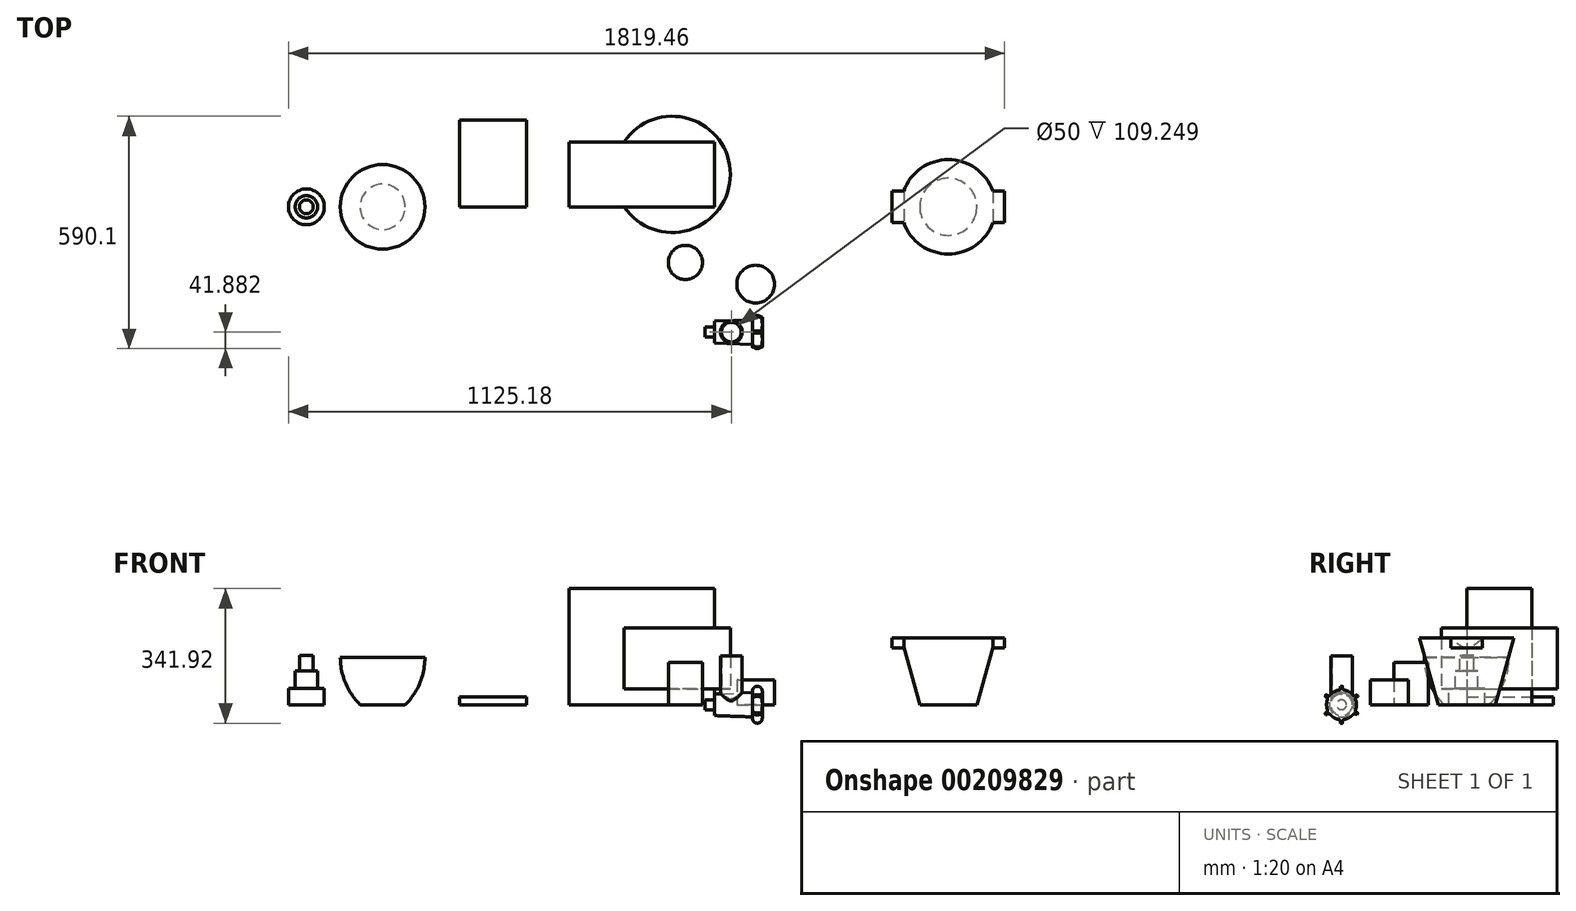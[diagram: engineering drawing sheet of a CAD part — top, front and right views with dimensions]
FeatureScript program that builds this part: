
annotation { "Feature Type Name" : "Feature", "Feature Type Description" : "" }
export const myFeature = defineFeature(function(context is Context, id is Id, definition is map)
    precondition{}
    {
        {
            var Q0;
            Q0=qCreatedBy(makeId("Top.planeOp"),FACE);
            var sketch = newSketch(context, id + "F0", { "sketchPlane" : qUnion([Q0])});
            skLineSegment(sketch, "E0.bottom", {"start": v(-647.77, 0) * mm, "end": v(-477.77, 0) * mm});
            skLineSegment(sketch, "E0.top", {"start": v(-647.77, 220) * mm, "end": v(-477.77, 220) * mm});
            skLineSegment(sketch, "E0.left", {"start": v(-647.77, 0) * mm, "end": v(-647.77, 220) * mm});
            skLineSegment(sketch, "E0.right", {"start": v(-477.77, 0) * mm, "end": v(-477.77, 220) * mm});
            skSolve(sketch);
        }
        {
            var Q0;
            Q0 = qSketchRegion(id + "F0", true);
            extrude(context, id + "F1", {"entities" : qUnion([Q0]), "depth" : 20 * mm});
        }
        {
            var Q0;
            Q0=qCreatedBy(makeId("Top.planeOp"),FACE);
            var sketch = newSketch(context, id + "F2", { "sketchPlane" : qUnion([Q0])});
            skLineSegment(sketch, "E1.bottom", {"start": v(0, 0) * mm, "end": v(-370, 0) * mm});
            skLineSegment(sketch, "E1.top", {"start": v(0, 165) * mm, "end": v(-370, 165) * mm});
            skLineSegment(sketch, "E1.left", {"start": v(0, 0) * mm, "end": v(0, 165) * mm});
            skLineSegment(sketch, "E1.right", {"start": v(-370, 0) * mm, "end": v(-370, 165) * mm});
            skSolve(sketch);
        }
        {
            var Q0;
            Q0 = qSketchRegion(id + "F2", true);
            extrude(context, id + "F3", {"entities" : qUnion([Q0]), "depth" : 40 * mm});
        }
        {
            var Q0;
            Q0=makeQuery(id+"F3.opExtrude","CAP_FACE",FACE,{"disambiguationData":[OSD([sQuery(id+"F2.wireOp",EDGE,"E1.bottom"),sQuery(id+"F2.wireOp",EDGE,"E1.top"),sQuery(id+"F2.wireOp",EDGE,"E1.left"),sQuery(id+"F2.wireOp",EDGE,"E1.right")])],"isStart":false});
            var sketch = newSketch(context, id + "F4", { "sketchPlane" : qUnion([Q0])});
            skArc(sketch, "E2", {"start": v(-229.77, 0) * mm, "mid": v(40, 82.5) * mm, "end": v(-229.77, 165) * mm});
            skLineSegment(sketch, "E3", {"start": v(0, 82.5) * mm, "end": v(-370, 82.5) * mm, "construction": true});
            skLineSegment(sketch, "E4", {"start": v(-229.77, 165) * mm, "end": v(-370, 165) * mm});
            skLineSegment(sketch, "E5", {"start": v(-370, 165) * mm, "end": v(-370, 0) * mm});
            skLineSegment(sketch, "E6", {"start": v(-370, 0) * mm, "end": v(-229.77, 0) * mm});
            skSolve(sketch);
        }
        {
            var Q0;
            Q0 = qSketchRegion(id + "F4", true);
            extrude(context, id + "F5", {"entities" : qUnion([Q0]), "operationType" : NewBodyOperationType.ADD, "depth" : 155 * mm});
        }
        {
            var Q0;
            Q0=makeQuery(id+"F5.opExtrude","CAP_FACE",FACE,{"disambiguationData":[OSD([sQuery(id+"F4.wireOp",EDGE,"E2"),sQuery(id+"F4.wireOp",EDGE,"E4"),sQuery(id+"F4.wireOp",EDGE,"E5"),sQuery(id+"F4.wireOp",EDGE,"E6")])],"isStart":false});
            var sketch = newSketch(context, id + "F6", { "sketchPlane" : qUnion([Q0])});
            skLineSegment(sketch, "E7.bottom", {"start": v(-370, 0) * mm, "end": v(0, 0) * mm});
            skLineSegment(sketch, "E7.top", {"start": v(-370, 165) * mm, "end": v(0, 165) * mm});
            skLineSegment(sketch, "E7.left", {"start": v(-370, 0) * mm, "end": v(-370, 165) * mm});
            skLineSegment(sketch, "E7.right", {"start": v(0, 0) * mm, "end": v(0, 165) * mm});
            skSolve(sketch);
        }
        {
            var Q0;
            Q0 = qSketchRegion(id + "F6", true);
            extrude(context, id + "F7", {"entities" : qUnion([Q0]), "operationType" : NewBodyOperationType.ADD, "depth" : 100 * mm});
        }
        {
            var Q0;
            Q0=qCreatedBy(makeId("Front.planeOp"),FACE);
            var sketch = newSketch(context, id + "F8", { "sketchPlane" : qUnion([Q0])});
            skLineSegment(sketch, "E8", {"start": v(593.64, 0) * mm, "end": v(593.64, 170) * mm});
            skLineSegment(sketch, "E9", {"start": v(593.64, 170) * mm, "end": v(713.64, 170) * mm});
            skLineSegment(sketch, "E10", {"start": v(713.64, 170) * mm, "end": v(666.14, 0) * mm});
            skLineSegment(sketch, "E11", {"start": v(666.14, 0) * mm, "end": v(593.64, 0) * mm});
            skSolve(sketch);
        }
        {
            var Q0;
            Q0=makeQuery(id+"F8.imprint","IMPRINT",FACE,{"disambiguationData":[TD([[makeQuery(id+"F8.imprint","IMPRINT",EDGE,{"derivedFrom":sQuery(id+"F8.wireOp",EDGE,"E8")}),-1.0]])]});
            var Q1;
            Q1=sQuery(id+"F8.wireOp",EDGE,"E8");
            revolve(context, id + "F9", {"entities" : qUnion([Q0]), "axis" : qUnion([Q1]), "revolveType" : RevolveType.FULL});
        }
        {
            var Q0;
            Q0=makeQuery(id+"F9.opRevolve","SWEPT_FACE",FACE,{"disambiguationData":[OSD([sQuery(id+"F8.wireOp",EDGE,"E9")])]});
            var sketch = newSketch(context, id + "F10", { "sketchPlane" : qUnion([Q0])});
            skLineSegment(sketch, "E12.bottom", {"start": v(480.5, 40) * mm, "end": v(450.5, 40) * mm});
            skLineSegment(sketch, "E12.top", {"start": v(480.5, -40) * mm, "end": v(450.5, -40) * mm});
            skLineSegment(sketch, "E12.left", {"start": v(480.5, 40) * mm, "end": v(480.5, -40) * mm});
            skLineSegment(sketch, "E12.right", {"start": v(450.5, 40) * mm, "end": v(450.5, -40) * mm});
            skLineSegment(sketch, "E13", {"start": v(593.64, 120) * mm, "end": v(593.64, -120) * mm, "construction": true});
            skLineSegment(sketch, "E14.MirrorCS", {"start": v(706.78, -40) * mm, "end": v(736.78, -40) * mm});
            skLineSegment(sketch, "E15.MirrorCS", {"start": v(706.78, 40) * mm, "end": v(706.78, -40) * mm});
            skLineSegment(sketch, "E16.MirrorCS", {"start": v(736.78, 40) * mm, "end": v(736.78, -40) * mm});
            skLineSegment(sketch, "E17.MirrorCS", {"start": v(706.78, 40) * mm, "end": v(736.78, 40) * mm});
            skSolve(sketch);
        }
        {
            var Q0;
            Q0 = qSketchRegion(id + "F10", true);
            extrude(context, id + "F11", {"entities" : qUnion([Q0]), "operationType" : NewBodyOperationType.ADD, "oppositeDirection" : true, "depth" : 25 * mm});
        }
        {
            var Q0;
            Q0=qCreatedBy(makeId("Top.planeOp"),FACE);
            var sketch = newSketch(context, id + "F12", { "sketchPlane" : qUnion([Q0])});
            skCircle(sketch, "E18", {"center": v(-74.2, -141.42) * mm, "radius": 43.5 * mm});
            skSolve(sketch);
        }
        {
            var Q0;
            Q0 = qSketchRegion(id + "F12", true);
            extrude(context, id + "F13", {"entities" : qUnion([Q0]), "depth" : 108 * mm});
        }
        {
            var Q0;
            Q0=qCreatedBy(makeId("Top.planeOp"),FACE);
            var sketch = newSketch(context, id + "F14", { "sketchPlane" : qUnion([Q0])});
            skCircle(sketch, "E19", {"center": v(104.26, -196.52) * mm, "radius": 48 * mm});
            skSolve(sketch);
        }
        {
            var Q0;
            Q0 = qSketchRegion(id + "F14", true);
            extrude(context, id + "F15", {"entities" : qUnion([Q0]), "depth" : 63 * mm});
        }
        {
            var Q0;
            Q0=qCreatedBy(makeId("Right.planeOp"),FACE);
            var sketch = newSketch(context, id + "F16", { "sketchPlane" : qUnion([Q0])});
            skCircle(sketch, "E20", {"center": v(-318.22, 0) * mm, "radius": 27.5 * mm});
            skSolve(sketch);
        }
        {
            var Q0;
            Q0=qCreatedBy(makeId("Right.planeOp"),FACE);
            cPlane(context, id + "F17", {"entities" : qUnion([Q0]), "cplaneType" : CPlaneType.OFFSET, "offset" : 96 * mm, "width" : 150 * mm, "height" : 150 * mm});
        }
        {
            var Q0;
            Q0=sQuery(id+"F16.wireOp",VERTEX,"E20.center");
            var Q1;
            Q1=qCreatedBy(makeId("Front.planeOp"),FACE);
            cPlane(context, id + "F18", {"entities" : qUnion([Q0, Q1]), "cplaneType" : CPlaneType.PLANE_POINT, "offset" : 25 * mm, "width" : 150 * mm, "height" : 150 * mm});
        }
        {
            var Q0;
            Q0=qCreatedBy(id+"F17.planeOp",FACE);
            var sketch = newSketch(context, id + "F19", { "sketchPlane" : qUnion([Q0])});
            skCircle(sketch, "E21", {"center": v(-318.22, 0) * mm, "radius": 31 * mm});
            skSolve(sketch);
        }
        {
            var Q0;
            Q0=makeQuery(id+"F16.imprint","IMPRINT",FACE,{"disambiguationData":[TD([[makeQuery(id+"F16.imprint","IMPRINT",EDGE,{"derivedFrom":sQuery(id+"F16.wireOp",EDGE,"E20")}),1.0]])]});
            var Q1;
            Q1=makeQuery(id+"F19.imprint","IMPRINT",FACE,{"disambiguationData":[TD([[makeQuery(id+"F19.imprint","IMPRINT",EDGE,{"derivedFrom":sQuery(id+"F19.wireOp",EDGE,"E21")}),1.0]])]});
            loft(context, id + "F20", {"sheetProfilesArray" : [{ "sheetProfileEntities" : qUnion([Q0]) }, { "sheetProfileEntities" : qUnion([Q1]) }]});
        }
        {
            var Q0;
            Q0=makeQuery(id+"F20.opLoft","CAP_FACE",FACE,{"disambiguationData":[OSD([makeQuery(id+"F19.imprint","IMPRINT",FACE,{"disambiguationData":[TD([[makeQuery(id+"F19.imprint","IMPRINT",EDGE,{"derivedFrom":sQuery(id+"F19.wireOp",EDGE,"E21")}),1.0]])]})])],"isStart":true});
            var sketch = newSketch(context, id + "F21", { "sketchPlane" : qUnion([Q0])});
            skArc(sketch, "E22", {"start": v(-320.72, 37.92) * mm, "mid": v(-337.22, 32.9) * mm, "end": v(-349.8, 21.12) * mm});
            skLineSegment(sketch, "E23", {"start": v(-320.72, 37.92) * mm, "end": v(-320.72, 46.92) * mm});
            skLineSegment(sketch, "E24", {"start": v(-320.72, 46.92) * mm, "end": v(-315.72, 46.92) * mm});
            skLineSegment(sketch, "E25", {"start": v(-315.72, 46.92) * mm, "end": v(-315.72, 37.92) * mm});
            skLineSegment(sketch, "E26.1.0", {"start": v(-352.3, 16.8) * mm, "end": v(-360.1, 21.3) * mm});
            skLineSegment(sketch, "E26.1.1", {"start": v(-360.1, 21.3) * mm, "end": v(-357.6, 25.62) * mm});
            skLineSegment(sketch, "E26.1.2", {"start": v(-357.6, 25.62) * mm, "end": v(-349.8, 21.12) * mm});
            skLineSegment(sketch, "E26.2.0", {"start": v(-349.8, -21.12) * mm, "end": v(-357.6, -25.62) * mm});
            skLineSegment(sketch, "E26.2.1", {"start": v(-357.6, -25.62) * mm, "end": v(-360.1, -21.3) * mm});
            skLineSegment(sketch, "E26.2.2", {"start": v(-360.1, -21.3) * mm, "end": v(-352.3, -16.8) * mm});
            skLineSegment(sketch, "E26.3.0", {"start": v(-315.72, -37.92) * mm, "end": v(-315.72, -46.92) * mm});
            skLineSegment(sketch, "E26.3.1", {"start": v(-315.72, -46.92) * mm, "end": v(-320.72, -46.92) * mm});
            skLineSegment(sketch, "E26.3.2", {"start": v(-320.72, -46.92) * mm, "end": v(-320.72, -37.92) * mm});
            skLineSegment(sketch, "E26.4.0", {"start": v(-284.13, -16.8) * mm, "end": v(-276.34, -21.3) * mm});
            skLineSegment(sketch, "E26.4.1", {"start": v(-276.34, -21.3) * mm, "end": v(-278.84, -25.62) * mm});
            skLineSegment(sketch, "E26.4.2", {"start": v(-278.84, -25.62) * mm, "end": v(-286.63, -21.12) * mm});
            skLineSegment(sketch, "E26.5.0", {"start": v(-286.63, 21.12) * mm, "end": v(-278.84, 25.62) * mm});
            skLineSegment(sketch, "E26.5.1", {"start": v(-278.84, 25.62) * mm, "end": v(-276.34, 21.3) * mm});
            skLineSegment(sketch, "E26.5.2", {"start": v(-276.34, 21.3) * mm, "end": v(-284.13, 16.8) * mm});
            skArc(sketch, "E27.trimOffspring", {"start": v(-352.3, 16.8) * mm, "mid": v(-356.22, 0) * mm, "end": v(-352.3, -16.8) * mm});
            skArc(sketch, "E28.trimOffspring", {"start": v(-349.8, -21.12) * mm, "mid": v(-337.22, -32.9) * mm, "end": v(-320.72, -37.92) * mm});
            skArc(sketch, "E29.trimOffspring", {"start": v(-315.72, -37.92) * mm, "mid": v(-299.22, -32.9) * mm, "end": v(-286.63, -21.12) * mm});
            skArc(sketch, "E30.trimOffspring", {"start": v(-284.13, -16.8) * mm, "mid": v(-280.22, 0) * mm, "end": v(-284.13, 16.8) * mm});
            skArc(sketch, "E31.trimOffspring", {"start": v(-286.63, 21.12) * mm, "mid": v(-299.22, 32.9) * mm, "end": v(-315.72, 37.92) * mm});
            skSolve(sketch);
        }
        {
            var Q0;
            Q0 = qSketchRegion(id + "F21", true);
            extrude(context, id + "F22", {"entities" : qUnion([Q0]), "operationType" : NewBodyOperationType.ADD, "depth" : 25 * mm});
        }
        {
            var Q0;
            Q0=makeQuery(id+"F22.opExtrude","CAP_EDGE",EDGE,{"disambiguationData":[OSD([sQuery(id+"F21.wireOp",EDGE,"E26.1.1")])],"isStart":true});
            var Q1;
            Q1=makeQuery(id+"F22.opExtrude","CAP_EDGE",EDGE,{"disambiguationData":[OSD([sQuery(id+"F21.wireOp",EDGE,"E26.1.1")])],"isStart":false});
            var Q2;
            Q2=makeQuery(id+"F22.opExtrude","CAP_EDGE",EDGE,{"disambiguationData":[OSD([sQuery(id+"F21.wireOp",EDGE,"E26.2.1")])],"isStart":true});
            var Q3;
            Q3=makeQuery(id+"F22.opExtrude","CAP_EDGE",EDGE,{"disambiguationData":[OSD([sQuery(id+"F21.wireOp",EDGE,"E26.2.1")])],"isStart":false});
            var Q4;
            Q4=makeQuery(id+"F22.opExtrude","CAP_EDGE",EDGE,{"disambiguationData":[OSD([sQuery(id+"F21.wireOp",EDGE,"E26.3.1")])],"isStart":false});
            var Q5;
            Q5=makeQuery(id+"F22.opExtrude","CAP_EDGE",EDGE,{"disambiguationData":[OSD([sQuery(id+"F21.wireOp",EDGE,"E26.3.1")])],"isStart":true});
            var Q6;
            Q6=makeQuery(id+"F22.opExtrude","CAP_EDGE",EDGE,{"disambiguationData":[OSD([sQuery(id+"F21.wireOp",EDGE,"E26.4.1")])],"isStart":true});
            var Q7;
            Q7=makeQuery(id+"F22.opExtrude","CAP_EDGE",EDGE,{"disambiguationData":[OSD([sQuery(id+"F21.wireOp",EDGE,"E26.4.1")])],"isStart":false});
            var Q8;
            Q8=makeQuery(id+"F22.opExtrude","CAP_EDGE",EDGE,{"disambiguationData":[OSD([sQuery(id+"F21.wireOp",EDGE,"E26.5.1")])],"isStart":true});
            var Q9;
            Q9=makeQuery(id+"F22.opExtrude","CAP_EDGE",EDGE,{"disambiguationData":[OSD([sQuery(id+"F21.wireOp",EDGE,"E26.5.1")])],"isStart":false});
            var Q10;
            Q10=makeQuery(id+"F22.opExtrude","CAP_EDGE",EDGE,{"disambiguationData":[OSD([sQuery(id+"F21.wireOp",EDGE,"E24")])],"isStart":true});
            var Q11;
            Q11=makeQuery(id+"F22.opExtrude","CAP_EDGE",EDGE,{"disambiguationData":[OSD([sQuery(id+"F21.wireOp",EDGE,"E24")])],"isStart":false});
            fillet(context, id + "F23", {"entities" : qUnion([Q0, Q1, Q2, Q3, Q4, Q5, Q6, Q7, Q8, Q9, Q10, Q11]), "radius" : (25 / 2) * mm, "tangentPropagation" : true, "allowEdgeOverflow" : false});
        }
        {
            var Q0;
            Q0=makeQuery(id+"F22.opExtrude","SWEPT_EDGE",EDGE,{"disambiguationData":[OSD([sQuery(id+"F21.wireOp",EDGE,"E26.2.2"),sQuery(id+"F21.wireOp",EDGE,"E27.trimOffspring")])]});
            var Q1;
            Q1=makeQuery(id+"F22.opExtrude","SWEPT_EDGE",EDGE,{"disambiguationData":[OSD([sQuery(id+"F21.wireOp",EDGE,"E26.1.0"),sQuery(id+"F21.wireOp",EDGE,"E27.trimOffspring")])]});
            var Q2;
            Q2=makeQuery(id+"F22.opExtrude","SWEPT_EDGE",EDGE,{"disambiguationData":[OSD([sQuery(id+"F21.wireOp",EDGE,"E22"),sQuery(id+"F21.wireOp",EDGE,"E26.1.2")])]});
            var Q3;
            Q3=makeQuery(id+"F22.opExtrude","SWEPT_EDGE",EDGE,{"disambiguationData":[OSD([sQuery(id+"F21.wireOp",EDGE,"E22"),sQuery(id+"F21.wireOp",EDGE,"E23")])]});
            var Q4;
            Q4=makeQuery(id+"F22.opExtrude","SWEPT_EDGE",EDGE,{"disambiguationData":[OSD([sQuery(id+"F21.wireOp",EDGE,"E25"),sQuery(id+"F21.wireOp",EDGE,"E31.trimOffspring")])]});
            var Q5;
            Q5=makeQuery(id+"F22.opExtrude","SWEPT_EDGE",EDGE,{"disambiguationData":[OSD([sQuery(id+"F21.wireOp",EDGE,"E26.5.0"),sQuery(id+"F21.wireOp",EDGE,"E31.trimOffspring")])]});
            var Q6;
            Q6=makeQuery(id+"F22.opExtrude","SWEPT_EDGE",EDGE,{"disambiguationData":[OSD([sQuery(id+"F21.wireOp",EDGE,"E26.5.2"),sQuery(id+"F21.wireOp",EDGE,"E30.trimOffspring")])]});
            var Q7;
            Q7=makeQuery(id+"F22.opExtrude","SWEPT_EDGE",EDGE,{"disambiguationData":[OSD([sQuery(id+"F21.wireOp",EDGE,"E26.4.0"),sQuery(id+"F21.wireOp",EDGE,"E30.trimOffspring")])]});
            var Q8;
            Q8=makeQuery(id+"F22.opExtrude","SWEPT_EDGE",EDGE,{"disambiguationData":[OSD([sQuery(id+"F21.wireOp",EDGE,"E26.4.2"),sQuery(id+"F21.wireOp",EDGE,"E29.trimOffspring")])]});
            var Q9;
            Q9=makeQuery(id+"F22.opExtrude","SWEPT_EDGE",EDGE,{"disambiguationData":[OSD([sQuery(id+"F21.wireOp",EDGE,"E26.3.0"),sQuery(id+"F21.wireOp",EDGE,"E29.trimOffspring")])]});
            var Q10;
            Q10=makeQuery(id+"F22.opExtrude","SWEPT_EDGE",EDGE,{"disambiguationData":[OSD([sQuery(id+"F21.wireOp",EDGE,"E26.3.2"),sQuery(id+"F21.wireOp",EDGE,"E28.trimOffspring")])]});
            var Q11;
            Q11=makeQuery(id+"F22.opExtrude","SWEPT_EDGE",EDGE,{"disambiguationData":[OSD([sQuery(id+"F21.wireOp",EDGE,"E26.2.0"),sQuery(id+"F21.wireOp",EDGE,"E28.trimOffspring")])]});
            fillet(context, id + "F24", {"entities" : qUnion([Q0, Q1, Q2, Q3, Q4, Q5, Q6, Q7, Q8, Q9, Q10, Q11]), "radius" : 5 * mm, "tangentPropagation" : true, "allowEdgeOverflow" : false});
        }
        {
            var Q0;
            Q0=makeQuery(id+"F20.opLoft","CAP_FACE",FACE,{"disambiguationData":[OSD([makeQuery(id+"F16.imprint","IMPRINT",FACE,{"disambiguationData":[TD([[makeQuery(id+"F16.imprint","IMPRINT",EDGE,{"derivedFrom":sQuery(id+"F16.wireOp",EDGE,"E20")}),1.0]])]})])],"isStart":true});
            var sketch = newSketch(context, id + "F25", { "sketchPlane" : qUnion([Q0])});
            skCircle(sketch, "E32", {"center": v(318.22, 0) * mm, "radius": 12.5 * mm});
            skSolve(sketch);
        }
        {
            var Q0;
            Q0 = qSketchRegion(id + "F25", true);
            extrude(context, id + "F26", {"entities" : qUnion([Q0]), "operationType" : NewBodyOperationType.ADD, "depth" : 25 * mm});
        }
        {
            var Q0;
            Q0=qCreatedBy(makeId("Top.planeOp"),FACE);
            var sketch = newSketch(context, id + "F27", { "sketchPlane" : qUnion([Q0])});
            skCircle(sketch, "E33", {"center": v(42.5, -318.22) * mm, "radius": 27.5 * mm});
            skCircle(sketch, "E34", {"center": v(42.5, -318.22) * mm, "radius": 25 * mm});
            skSolve(sketch);
        }
        {
            var Q0;
            Q0 = qSketchRegion(id + "F27", true);
            extrude(context, id + "F28", {"entities" : qUnion([Q0]), "operationType" : NewBodyOperationType.ADD, "depth" : (97 + 54 / 2) * mm});
        }
        {
            var Q0;
            Q0=qCreatedBy(makeId("Front.planeOp"),FACE);
            var sketch = newSketch(context, id + "F29", { "sketchPlane" : qUnion([Q0])});
            skLineSegment(sketch, "E35", {"start": v(-843.41, 0) * mm, "end": v(-900.91, 0) * mm});
            skLineSegment(sketch, "E36", {"start": v(-950.91, 120) * mm, "end": v(-843.41, 120) * mm});
            skLineSegment(sketch, "E37", {"start": v(-843.41, 120) * mm, "end": v(-843.41, 0) * mm});
            skArc(sketch, "E38", {"start": v(-950.91, 120) * mm, "mid": v(-937.73, 55.08) * mm, "end": v(-900.91, 0) * mm});
            skSolve(sketch);
        }
        {
            var Q0;
            Q0=makeQuery(id+"F29.imprint","IMPRINT",FACE,{"disambiguationData":[TD([[makeQuery(id+"F29.imprint","IMPRINT",EDGE,{"derivedFrom":sQuery(id+"F29.wireOp",EDGE,"E35")}),-1.0]])]});
            var Q1;
            Q1=sQuery(id+"F29.wireOp",EDGE,"E37");
            revolve(context, id + "F30", {"entities" : qUnion([Q0]), "axis" : qUnion([Q1]), "revolveType" : RevolveType.FULL});
        }
        {
            var Q0;
            Q0=qCreatedBy(makeId("Front.planeOp"),FACE);
            var sketch = newSketch(context, id + "F31", { "sketchPlane" : qUnion([Q0])});
            skLineSegment(sketch, "E39", {"start": v(-1082.68, 0) * mm, "end": v(-1082.68, 42) * mm});
            skLineSegment(sketch, "E40", {"start": v(-1082.68, 42) * mm, "end": v(-1065.68, 42) * mm});
            skLineSegment(sketch, "E41", {"start": v(-1065.68, 42) * mm, "end": v(-1065.68, 86) * mm});
            skLineSegment(sketch, "E42", {"start": v(-1065.68, 86) * mm, "end": v(-1054.68, 86) * mm});
            skLineSegment(sketch, "E43", {"start": v(-1054.68, 86) * mm, "end": v(-1054.68, 125) * mm});
            skLineSegment(sketch, "E44", {"start": v(-1054.68, 125) * mm, "end": v(-1037.18, 125) * mm});
            skLineSegment(sketch, "E45", {"start": v(-1037.18, 125) * mm, "end": v(-1037.18, 0) * mm});
            skLineSegment(sketch, "E46", {"start": v(-1037.18, 0) * mm, "end": v(-1082.68, 0) * mm});
            skSolve(sketch);
        }
        {
            var Q0;
            Q0 = qSketchRegion(id + "F31", true);
            var Q1;
            Q1=sQuery(id+"F31.wireOp",EDGE,"E45");
            revolve(context, id + "F32", {"entities" : qUnion([Q0]), "axis" : qUnion([Q1]), "revolveType" : RevolveType.FULL});
        }
    });
